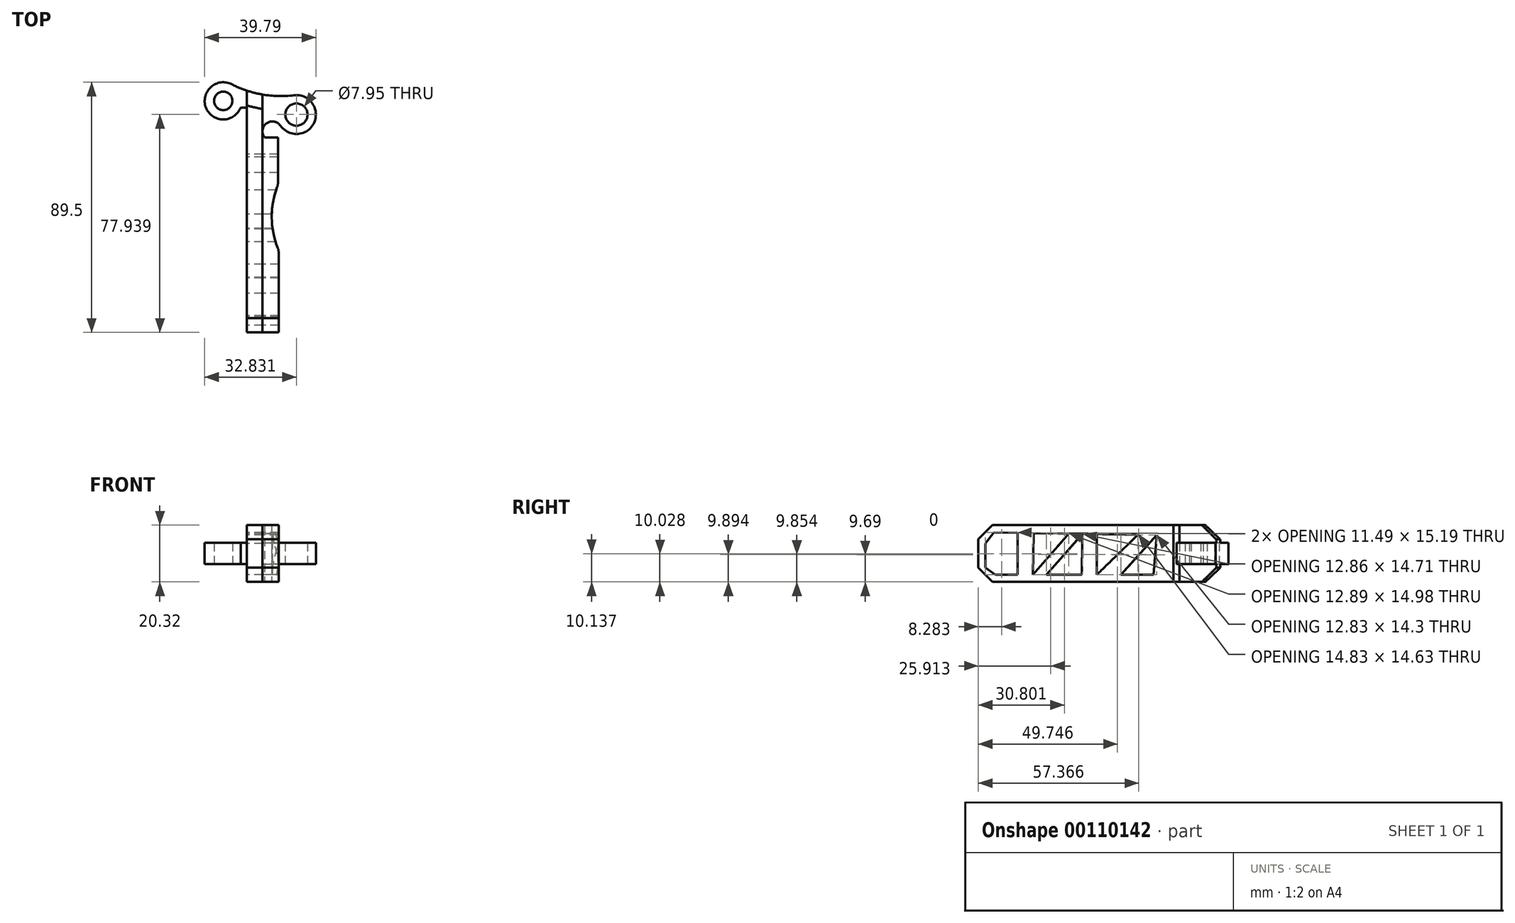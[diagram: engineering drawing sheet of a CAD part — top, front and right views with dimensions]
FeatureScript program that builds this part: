
annotation { "Feature Type Name" : "Feature", "Feature Type Description" : "" }
export const myFeature = defineFeature(function(context is Context, id is Id, definition is map)
    precondition{}
    {
        {
            var Q0;
            Q0=qCreatedBy(makeId("Top.planeOp"),FACE);
            var sketch = newSketch(context, id + "F0", { "sketchPlane" : qUnion([Q0])});
            skCircle(sketch, "E0", {"center": v(-37.9, 40.51) * mm, "radius": 6.65 * mm});
            skCircle(sketch, "E1", {"center": v(-11.72, 35.6) * mm, "radius": 6.96 * mm});
            skArc(sketch, "E2", {"start": v(-17.44, 31.65) * mm, "mid": v(-22.44, 32.47) * mm, "end": v(-23.09, 27.45) * mm});
            skArc(sketch, "E3", {"start": v(-34.87, 46.44) * mm, "mid": v(-24.01, 42.81) * mm, "end": v(-12.57, 42.51) * mm});
            skLineSegment(sketch, "E4", {"start": v(-29.48, 33.86) * mm, "end": v(-29.48, 38.12) * mm});
            skLineSegment(sketch, "E5", {"start": v(-29.48, 38.12) * mm, "end": v(-23.86, 38.12) * mm});
            skLineSegment(sketch, "E6", {"start": v(-23.86, 38.12) * mm, "end": v(-23.86, -42.33) * mm});
            skLineSegment(sketch, "E7", {"start": v(-23.86, -42.33) * mm, "end": v(-29.48, -42.33) * mm});
            skLineSegment(sketch, "E8", {"start": v(-29.48, -42.33) * mm, "end": v(-29.48, 33.86) * mm});
            skLineSegment(sketch, "E9", {"start": v(-29.48, 38.12) * mm, "end": v(-29.48, 44.19) * mm});
            skLineSegment(sketch, "E10", {"start": v(-23.86, 38.12) * mm, "end": v(-23.86, 42.78) * mm});
            skLineSegment(sketch, "E11", {"start": v(-29.48, -34.94) * mm, "end": v(-23.86, -34.94) * mm});
            skCircle(sketch, "E12", {"center": v(-37.9, 40.51) * mm, "radius": 3.29 * mm});
            skCircle(sketch, "E13", {"center": v(-11.72, 35.6) * mm, "radius": 3.98 * mm});
            skLineSegment(sketch, "E14", {"start": v(-31.69, 38.12) * mm, "end": v(-29.48, 38.12) * mm});
            skLineSegment(sketch, "E15", {"start": v(-23.09, 27.45) * mm, "end": v(-18.3, 27.45) * mm});
            skLineSegment(sketch, "E16", {"start": v(-18.3, 27.45) * mm, "end": v(-18.3, 10.44) * mm});
            skLineSegment(sketch, "E17", {"start": v(-23.86, -42.33) * mm, "end": v(-18.06, -42.33) * mm});
            skLineSegment(sketch, "E18", {"start": v(-18.06, -42.33) * mm, "end": v(-18.06, -12.94) * mm});
            skArc(sketch, "E19", {"start": v(-18.3, 10.44) * mm, "mid": v(-20.55, -1.27) * mm, "end": v(-18.06, -12.94) * mm});
            skSolve(sketch);
        }
        {
            var Q0;
            {var subQ4=sQuery(id+"F0.wireOp",EDGE,"E4");Q0=makeQuery(id+"F0.imprint","IMPRINT",FACE,{"disambiguationData":[TD([[makeQuery(id+"F0.imprint","IMPRINT",EDGE,{"derivedFrom":subQ4}),-1.0]])]});}
            var Q1;
            Q1=makeQuery(id+"F0.imprint","IMPRINT",FACE,{"disambiguationData":[TD([[makeQuery(id+"F0.imprint","IMPRINT",EDGE,{"derivedFrom":sQuery(id+"F0.wireOp",EDGE,"E5")}),1.0]])]});
            var Q2;
            {var subQ0=sQuery(id+"F0.wireOp",EDGE,"E7");Q2=makeQuery(id+"F0.imprint","IMPRINT",FACE,{"disambiguationData":[TD([[makeQuery(id+"F0.imprint","IMPRINT",EDGE,{"derivedFrom":subQ0}),-1.0]])]});}
            extrude(context, id + "F1", {"entities" : qUnion([Q0, Q1, Q2]), "endBound" : BoundingType.SYMMETRIC, "depth" : 20.32 * mm});
        }
        {
            var Q0;
            Q0=makeQuery(id+"F0.imprint","IMPRINT",FACE,{"disambiguationData":[TD([[makeQuery(id+"F0.imprint","IMPRINT",EDGE,{"derivedFrom":sQuery(id+"F0.wireOp",EDGE,"E12")}),-1.0]])]});
            var Q1;
            Q1=makeQuery(id+"F0.imprint","IMPRINT",FACE,{"disambiguationData":[TD([[makeQuery(id+"F0.imprint","IMPRINT",EDGE,{"derivedFrom":sQuery(id+"F0.wireOp",EDGE,"E13")}),-1.0]])]});
            var Q2;
            {var subQ0=sQuery(id+"F0.wireOp",EDGE,"E10");Q2=makeQuery(id+"F0.imprint","IMPRINT",FACE,{"disambiguationData":[TD([[makeQuery(id+"F0.imprint","IMPRINT",EDGE,{"derivedFrom":subQ0}),-1.0]])]});}
            var Q3;
            {var subQ4=sQuery(id+"F0.wireOp",EDGE,"E9");Q3=makeQuery(id+"F0.imprint","IMPRINT",FACE,{"disambiguationData":[TD([[makeQuery(id+"F0.imprint","IMPRINT",EDGE,{"derivedFrom":subQ4}),1.0]])]});}
            extrude(context, id + "F2", {"entities" : qUnion([Q0, Q1, Q2, Q3]), "operationType" : NewBodyOperationType.ADD, "endBound" : BoundingType.SYMMETRIC, "depth" : 7.62 * mm});
        }
        {
            var Q0;
            Q0=makeQuery(id+"F1.opExtrude","CAP_EDGE",EDGE,{"disambiguationData":[OSD([sQuery(id+"F0.wireOp",EDGE,"E3")])],"isStart":false});
            var Q1;
            Q1=makeQuery(id+"F1.opExtrude","CAP_EDGE",EDGE,{"disambiguationData":[OSD([sQuery(id+"F0.wireOp",EDGE,"E3")])],"isStart":true});
            var Q2;
            Q2=makeQuery(id+"F1.opExtrude","CAP_EDGE",EDGE,{"disambiguationData":[OSD([sQuery(id+"F0.wireOp",EDGE,"E7")])],"isStart":false});
            var Q3;
            Q3=makeQuery(id+"F1.opExtrude","CAP_EDGE",EDGE,{"disambiguationData":[OSD([sQuery(id+"F0.wireOp",EDGE,"E7")])],"isStart":true});
            chamfer(context, id + "F3", {"entities" : qUnion([Q0, Q1, Q2, Q3]), "width" : 5.08 * mm, "tangentPropagation" : true});
        }
        {
            var Q0;
            {var subQ0=sQuery(id+"F0.wireOp",EDGE,"E15");Q0=makeQuery(id+"F0.imprint","IMPRINT",FACE,{"disambiguationData":[TD([[makeQuery(id+"F0.imprint","IMPRINT",EDGE,{"derivedFrom":subQ0}),-1.0]])]});}
            extrude(context, id + "F4", {"entities" : qUnion([Q0]), "endBound" : BoundingType.SYMMETRIC, "depth" : 20.32 * mm});
        }
        {
            var Q0;
            Q0=makeQuery(id+"F4.opExtrude","CAP_EDGE",EDGE,{"disambiguationData":[OSD([sQuery(id+"F0.wireOp",EDGE,"E17")])],"isStart":false});
            var Q1;
            Q1=makeQuery(id+"F4.opExtrude","CAP_EDGE",EDGE,{"disambiguationData":[OSD([sQuery(id+"F0.wireOp",EDGE,"E17")])],"isStart":true});
            chamfer(context, id + "F5", {"entities" : qUnion([Q0, Q1]), "width" : 5.08 * mm, "tangentPropagation" : true});
        }
        {
            var Q0;
            Q0=makeQuery(id+"F4.opExtrude","SWEPT_EDGE",EDGE,{"disambiguationData":[OSD([sQuery(id+"F0.wireOp",EDGE,"E16"),sQuery(id+"F0.wireOp",EDGE,"E19")])]});
            var Q1;
            Q1=makeQuery(id+"F4.opExtrude","SWEPT_EDGE",EDGE,{"disambiguationData":[OSD([sQuery(id+"F0.wireOp",EDGE,"E18"),sQuery(id+"F0.wireOp",EDGE,"E19")])]});
            var Q2;
            Q2=makeQuery(id+"F2.opExtrude","SWEPT_EDGE",EDGE,{"disambiguationData":[OSD([sQuery(id+"F0.wireOp",EDGE,"E1"),sQuery(id+"F0.wireOp",EDGE,"E2")])]});
            var Q3;
            Q3=makeQuery(id+"F2.opExtrude","SWEPT_EDGE",EDGE,{"disambiguationData":[OSD([sQuery(id+"F0.wireOp",EDGE,"E1"),sQuery(id+"F0.wireOp",EDGE,"E3")])]});
            var Q4;
            Q4=makeQuery(id+"F2.opExtrude","SWEPT_EDGE",EDGE,{"disambiguationData":[OSD([sQuery(id+"F0.wireOp",EDGE,"E0"),sQuery(id+"F0.wireOp",EDGE,"E3")])]});
            var Q5;
            Q5=makeQuery(id+"F2.opExtrude","SWEPT_EDGE",EDGE,{"disambiguationData":[OSD([sQuery(id+"F0.wireOp",EDGE,"E4"),sQuery(id+"F0.wireOp",EDGE,"E5"),sQuery(id+"F0.wireOp",EDGE,"E9"),sQuery(id+"F0.wireOp",EDGE,"E14")])]});
            fillet(context, id + "F6", {"entities" : qUnion([Q0, Q1, Q2, Q3, Q4, Q5]), "radius" : 5.08 * mm, "tangentPropagation" : true, "allowEdgeOverflow" : false});
        }
        {
            var Q0;
            Q0=makeQuery(id+"F1.opExtrude","SWEPT_FACE",FACE,{"disambiguationData":[OSD([sQuery(id+"F0.wireOp",EDGE,"E8")])]});
            var sketch = newSketch(context, id + "F7", { "sketchPlane" : qUnion([Q0])});
            skLineSegment(sketch, "E20", {"start": v(39.8, 7.62) * mm, "end": v(-33.86, 6.49) * mm, "construction": true});
            skLineSegment(sketch, "E21", {"start": v(39.8, -7.62) * mm, "end": v(-33.86, -7.62) * mm, "construction": true});
            skPoint(sketch, "E21.endSnap0", {"position": v(-33.86, 0) * mm});
            skLineSegment(sketch, "E22", {"start": v(39.8, -5) * mm, "end": v(39.8, 3.62) * mm});
            skLineSegment(sketch, "E23", {"start": v(39.8, 3.62) * mm, "end": v(36.75, 7.57) * mm});
            skLineSegment(sketch, "E24", {"start": v(36.75, 7.57) * mm, "end": v(28.3, 7.44) * mm});
            skLineSegment(sketch, "E25", {"start": v(28.3, 7.44) * mm, "end": v(28.3, -7.62) * mm});
            skLineSegment(sketch, "E26", {"start": v(28.3, -7.62) * mm, "end": v(36.35, -7.62) * mm});
            skLineSegment(sketch, "E27", {"start": v(36.35, -7.62) * mm, "end": v(39.8, -5) * mm});
            skLineSegment(sketch, "E28", {"start": v(22.86, -7.62) * mm, "end": v(22.63, 7.36) * mm});
            skLineSegment(sketch, "E29", {"start": v(22.63, 7.36) * mm, "end": v(9.97, 7.16) * mm});
            skLineSegment(sketch, "E30", {"start": v(9.97, 7.16) * mm, "end": v(22.86, -7.62) * mm});
            skLineSegment(sketch, "E31", {"start": v(5.1, 7.09) * mm, "end": v(5.32, -7.62) * mm});
            skLineSegment(sketch, "E32", {"start": v(5.32, -7.62) * mm, "end": v(17.96, -7.62) * mm});
            skLineSegment(sketch, "E33", {"start": v(17.96, -7.62) * mm, "end": v(5.1, 7.09) * mm});
            skLineSegment(sketch, "E34", {"start": v(0, 7) * mm, "end": v(0, -7.62) * mm});
            skLineSegment(sketch, "E35", {"start": v(0, -7.62) * mm, "end": v(-14.83, 6.78) * mm});
            skLineSegment(sketch, "E36", {"start": v(-14.83, 6.78) * mm, "end": v(0, 7) * mm});
            skLineSegment(sketch, "E37", {"start": v(-20.37, -7.62) * mm, "end": v(-8.62, -7.62) * mm});
            skLineSegment(sketch, "E38", {"start": v(-8.62, -7.62) * mm, "end": v(-21.45, 6.68) * mm});
            skLineSegment(sketch, "E39", {"start": v(-21.45, 6.68) * mm, "end": v(-20.37, -7.62) * mm});
            skSolve(sketch);
        }
        {
            var Q0;
            Q0 = qSketchRegion(id + "F7", true);
            extrude(context, id + "F8", {"entities" : qUnion([Q0]), "operationType" : NewBodyOperationType.REMOVE, "oppositeDirection" : true, "depth" : 12.7 * mm});
        }
    });
